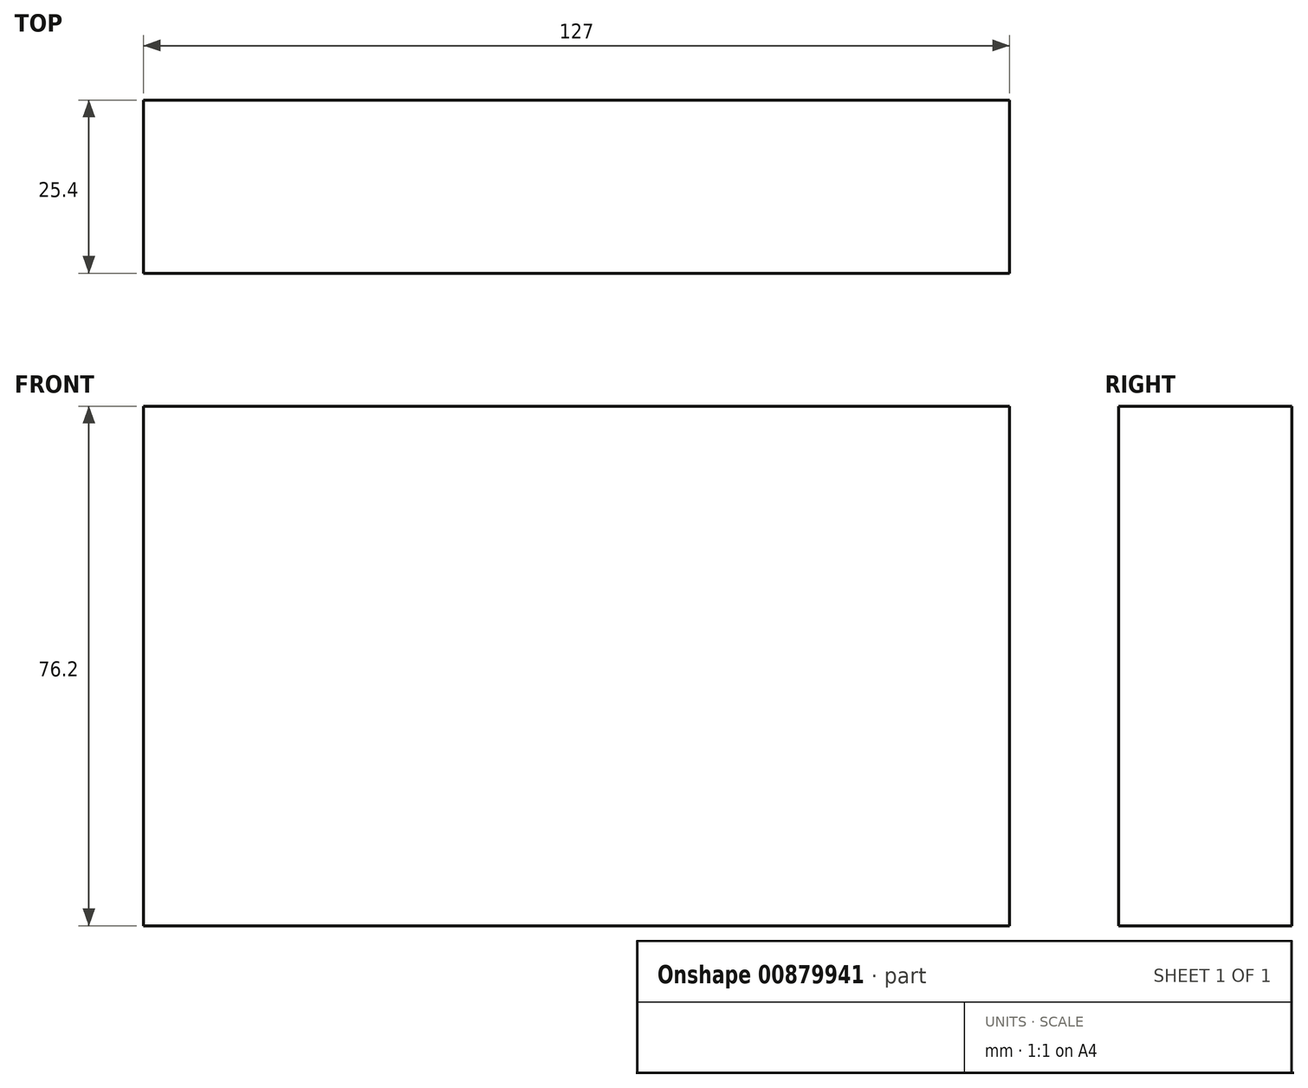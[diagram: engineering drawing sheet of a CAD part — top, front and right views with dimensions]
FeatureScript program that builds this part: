
annotation { "Feature Type Name" : "Feature", "Feature Type Description" : "" }
export const myFeature = defineFeature(function(context is Context, id is Id, definition is map)
    precondition{}
    {
        {
            var Q0;
            Q0=qCreatedBy(makeId("Front.planeOp"),FACE);
            var sketch = newSketch(context, id + "F0", { "sketchPlane" : qUnion([Q0])});
            skLineSegment(sketch, "E0.bottom", {"start": v(63.5, -38.1) * mm, "end": v(-63.5, -38.1) * mm});
            skLineSegment(sketch, "E0.top", {"start": v(63.5, 38.1) * mm, "end": v(-63.5, 38.1) * mm});
            skLineSegment(sketch, "E0.left", {"start": v(63.5, -38.1) * mm, "end": v(63.5, 38.1) * mm});
            skLineSegment(sketch, "E0.right", {"start": v(-63.5, -38.1) * mm, "end": v(-63.5, 38.1) * mm});
            skPoint(sketch, "E0.middle", {"position": v(0, 0) * mm});
            skSolve(sketch);
        }
        {
            var Q0;
            Q0 = qSketchRegion(id + "F0", true);
            extrude(context, id + "F1", {"entities" : qUnion([Q0]), "depth" : 25.4 * mm, "offsetDistance" : 25.4 * mm});
        }
    });
